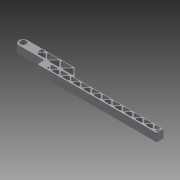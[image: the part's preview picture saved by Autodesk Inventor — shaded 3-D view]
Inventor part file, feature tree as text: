
AUTODESK INVENTOR PART (.ipt)
format: ipt  version: 2011 SP2 (Build 150309200, 309)  size: 967,168 bytes
history: native  units: mm
features: fillet x13, extrude x9, projected_geometry x8, sketch x7, plane x1, mirror x1
ambient origin geometry x8: Origin, YZ Plane, XZ Plane, XY Plane, X Axis, Y Axis, Z Axis, Center Point
feature tree (39):
  sketch  "Sketch1"  dims[d14=1.0mm d16=1.0mm]
  extrude  "Extrusion11"  Depth=1.0mm
  extrude  "Extrusion12"  Depth=1.0mm
  extrude  "Extrusion13"  Depth=16.580628mm
  extrude  "Extrusion14"  Depth=0.5mm
  extrude  "Extrusion15"  Depth=0.5mm
  extrude  "Extrusion16"  Depth=0.5mm
  fillet  "Fillet13"  Radius=0.5mm
  fillet  "Fillet14"  Radius=0.5mm
  fillet  "Fillet15"  Radius=0.5mm
  fillet  "Fillet16"  Radius=0.5mm
  fillet  "Fillet17"  Radius=0.5mm
  fillet  "Fillet18"  Radius=0.5mm
  fillet  "Fillet19"  Radius=0.5mm
  fillet  "Fillet20"  Radius=0.5mm
  fillet  "Fillet21"  Radius=0.5mm
  fillet  "Fillet22"  Radius=0.5mm
  fillet  "Fillet25"  Radius=0.5mm
  extrude  "Extrusion17"  Depth=0.5mm
  fillet  "Fillet26"  Radius=0.5mm
  extrude  "Extrusion18"  Depth=0.5mm
  fillet  "Fillet27"  Radius=0.5mm
  plane  "Work Plane2"
  mirror  "Mirror2"
  extrude  "Extrusion19"  Depth=0.5mm
  sketch  "Sketch11"  dims[d23=1.0mm d24=1.0mm]
  projected_geometry  "Projected Loop7"
  sketch  "Sketch12"  dims[d25=1.0mm d30=16.580628mm]
  projected_geometry  "Projected Loop8"
  projected_geometry  "Projected Loop9"
  sketch  "Sketch13"  dims[d32=1.0mm d62=0.5mm]
  sketch  "Sketch14"  dims[d64=0.5mm d65=0.5mm]
  sketch  "Sketch15"  dims[d66=0.5mm d68=0.5mm d69=0.5mm d70=0.5mm d71=0.5mm d72=0.5mm d73=0.5mm d74=0.5mm d75=0.5mm d76=0.5mm d77=0.5mm d78=0.5mm d79=0.5mm]
  projected_geometry  "Projected Loop10"
  projected_geometry  "Projected Loop11"
  projected_geometry  "Projected Loop12"
  projected_geometry  "Projected Loop13"
  projected_geometry  "Projected Loop14"
  sketch  "Sketch16"  dims[d80=0.5mm d81=0.5mm d82=0.5mm d83=0.5mm d84=0.5mm d85=0.5mm d86=0.5mm d87=0.5mm d88=0.5mm d89=0.5mm d90=0.5mm d91=0.5mm d92=0.5mm d93=0.5mm d94=0.5mm d95=0.5mm d96=0.5mm d97=0.5mm d98=0.5mm d99=0.5mm d100=0.5mm d101=0.5mm d102=0.5mm d103=0.5mm d104=0.5mm d106=0.5mm d107=0.5mm d108=0.5mm d109=0.5mm d115=14.209mm d116=3.912mm d120=5.45mm d121=3.75mm d122=1.875mm d124=2.725mm d126=3.060539mm d166=1.0mm d167=0.5mm d169=0.5mm d171=0.5mm d172=0.5mm d173=0.5mm d174=0.5mm d175=0.5mm d176=0.5mm d177=0.5mm d178=0.5mm d179=0.5mm d180=0.5mm d181=0.5mm d182=0.5mm d183=13.0mm d184=5.0mm d185=10.0mm d186=3.45mm d187=1.956mm d188=28.816511mm d189=34.516421mm d190=9.0mm d191=1.0mm d192=172.0mm d193=35.152794mm d194=10.0mm d195=0.0mm d196=10.0mm d197=0.0mm d198=6.85mm d199=0.0mm d200=10.0mm d201=8.0mm d202=0.0mm d203=14.835299mm d204=10.0mm d205=0.0mm d206=16.580628mm d207=10.0mm d208=0.0mm d209=1.0mm d210=1.0mm d211=0.5mm d212=1.75mm d213=0.2mm d214=1.0mm d215=0.5mm d216=0.5mm d217=0.5mm d218=1.0mm d221=2.25mm d222=10.0mm d223=0.0mm d224=0.75mm d225=10.0mm d226=0.0mm d227=0.5mm d228=-175.0mm d229=11.0mm d230=1.0mm d231=0.0mm d232=0.0mm]
